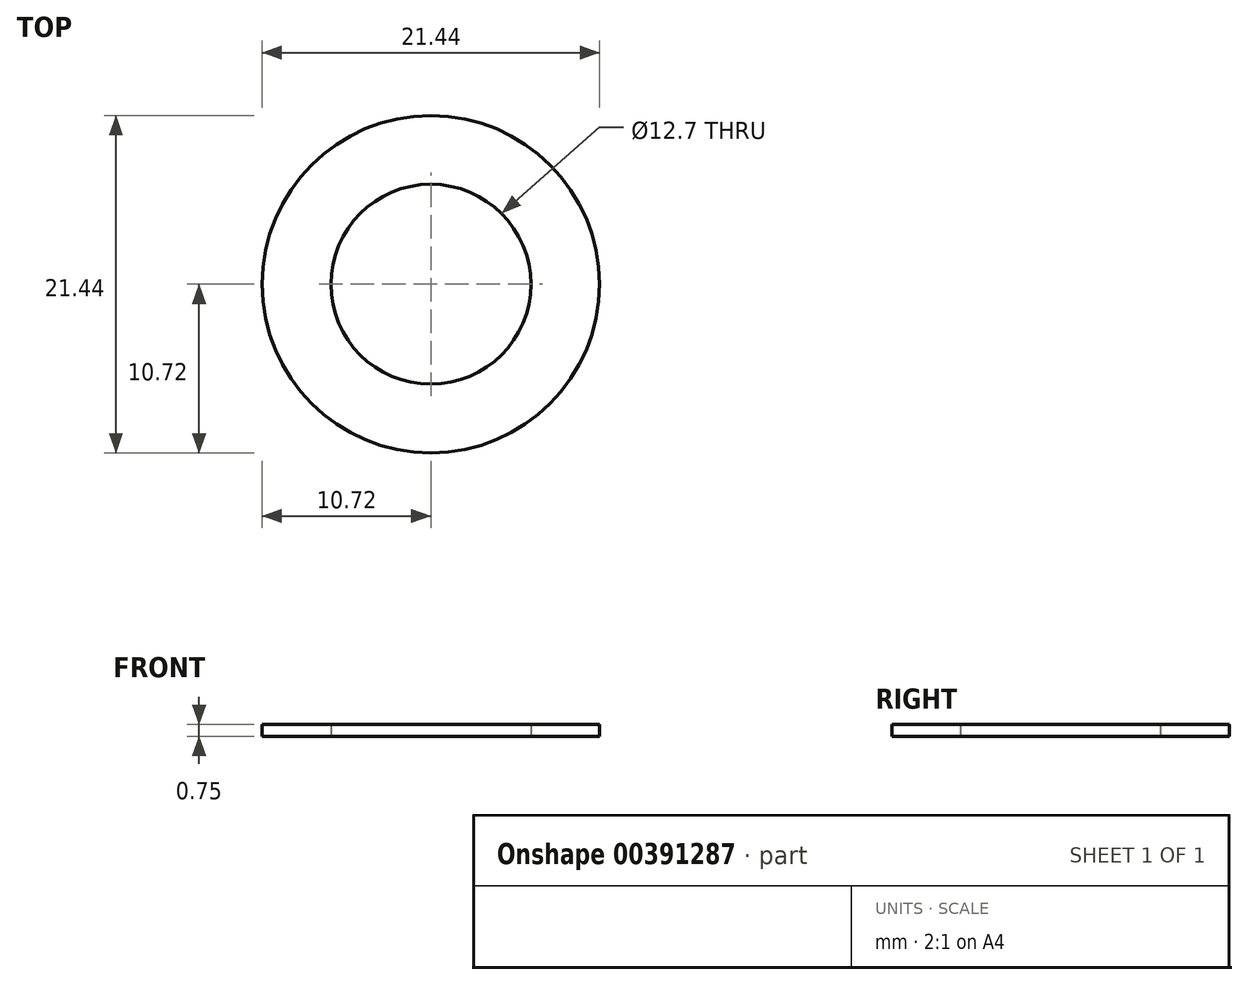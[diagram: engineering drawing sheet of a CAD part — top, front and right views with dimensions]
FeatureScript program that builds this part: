
annotation { "Feature Type Name" : "Feature", "Feature Type Description" : "" }
export const myFeature = defineFeature(function(context is Context, id is Id, definition is map)
    precondition{}
    {
        {
            assignVariable(context, id + "F0", {"name" : "Length", "anyValue" : .75});
        }
        {
            var Q0;
            Q0=qCreatedBy(makeId("Top.planeOp"),FACE);
            var sketch = newSketch(context, id + "F1", { "sketchPlane" : qUnion([Q0])});
            skCircle(sketch, "E0", {"center": v(0, 0) * mm, "radius": 10.72 * mm});
            skCircle(sketch, "E1", {"center": v(0, 0) * mm, "radius": 6.35 * mm});
            skSolve(sketch);
        }
        {
            var Q0;
            Q0=makeQuery(id+"F1.imprint","IMPRINT",FACE,{"disambiguationData":[TD([[makeQuery(id+"F1.imprint","IMPRINT",EDGE,{"derivedFrom":sQuery(id+"F1.wireOp",EDGE,"E0")}),1.0]])]});
            extrude(context, id + "F2", {"entities" : qUnion([Q0]), "depth" : (getVariable(context, 'Length')) * mm});
        }
    });
